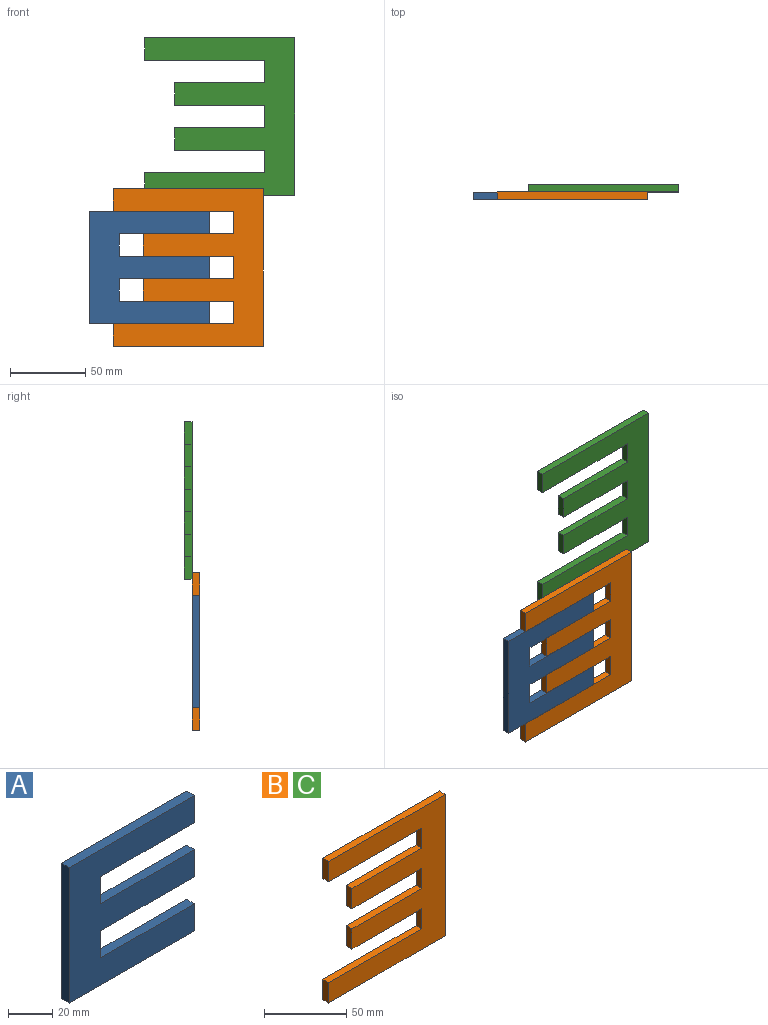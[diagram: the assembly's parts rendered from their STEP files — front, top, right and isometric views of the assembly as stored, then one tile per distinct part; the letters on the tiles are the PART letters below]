
ASSEMBLY  parts=3 mates=3
PART A: 14 faces, bbox 80x5x75 mm
  f0: plane 15x5mm, normal (1,0,0), area 75mm2, adj f1,f11,f12,f13
  f1: plane 60x5mm, normal (0,0,-1), area 300mm2, adj f0,f2,f12,f13
  f2: plane 15x5mm, normal (1,0,0), area 75mm2, adj f1,f3,f12,f13
  f3: plane 60x5mm, normal (0,0,1), area 300mm2, adj f2,f4,f12,f13
  f4: plane 15x5mm, normal (1,0,0), area 75mm2, adj f3,f5,f12,f13
  f5: plane 60x5mm, normal (0,0,-1), area 300mm2, adj f4,f6,f12,f13
  f6: plane 15x5mm, normal (1,0,0), area 75mm2, adj f5,f7,f12,f13
  f7: plane 80x5mm, normal (0,0,1), area 400mm2, adj f6,f8,f12,f13
  f8: plane 75x5mm, normal (-1,0,0), area 375mm2, adj f7,f9,f12,f13
  f9: plane 80x5mm, normal (0,0,-1), area 400mm2, adj f8,f10,f12,f13
  f10: plane 15x5mm, normal (1,0,0), area 75mm2, adj f9,f11,f12,f13
  f11: plane 60x5mm, normal (0,0,1), area 300mm2, adj f0,f10,f12,f13
  f12: plane 80x75mm, normal (0,-1,0), area 4200mm2, adj f0,f1,f2,f3,f4,f5,f6,f7
  f13: plane 80x75mm, normal (0,1,0), area 4200mm2, adj f0,f1,f2,f3,f4,f5,f6,f7
PART B: 18 faces, bbox 100x5x105 mm
  f0: plane 60x5mm, normal (0,0,1), area 300mm2, adj f1,f15,f16,f17
  f1: plane 15x5mm, normal (-1,0,0), area 75mm2, adj f0,f2,f16,f17
  f2: plane 60x5mm, normal (0,0,-1), area 300mm2, adj f1,f3,f16,f17
  f3: plane 15x5mm, normal (-1,0,0), area 75mm2, adj f2,f4,f16,f17
  f4: plane 80x5mm, normal (0,0,1), area 400mm2, adj f3,f5,f16,f17
  f5: plane 15x5mm, normal (-1,0,0), area 75mm2, adj f4,f6,f16,f17
  f6: plane 100x5mm, normal (0,0,-1), area 500mm2, adj f5,f7,f16,f17
  f7: plane 105x5mm, normal (1,0,0), area 525mm2, adj f6,f8,f16,f17
  f8: plane 100x5mm, normal (0,0,1), area 500mm2, adj f7,f9,f16,f17
  f9: plane 15x5mm, normal (-1,0,0), area 75mm2, adj f8,f10,f16,f17
  f10: plane 80x5mm, normal (0,0,-1), area 400mm2, adj f9,f11,f16,f17
  f11: plane 15x5mm, normal (-1,0,0), area 75mm2, adj f10,f12,f16,f17
  f12: plane 60x5mm, normal (0,0,1), area 300mm2, adj f11,f13,f16,f17
  f13: plane 15x5mm, normal (-1,0,0), area 75mm2, adj f12,f14,f16,f17
  f14: plane 60x5mm, normal (0,0,-1), area 300mm2, adj f13,f15,f16,f17
  f15: plane 15x5mm, normal (-1,0,0), area 75mm2, adj f0,f14,f16,f17
  f16: plane 105x100mm, normal (0,-1,0), area 6300mm2, adj f0,f1,f2,f3,f4,f5,f6,f7
  f17: plane 105x100mm, normal (0,1,0), area 6300mm2, adj f0,f1,f2,f3,f4,f5,f6,f7
PART C: same geometry as B
PLACE A t=(-104.59,-55.61,-10.92)mm
PLACE B t=(-95.25,-55.61,-11.6)mm fixed
PLACE C t=(-74.43,-50.61,89.04)mm
MATE planar B.f17 <-> C.f16  axis (0,1,0) through (-56.17,-55.61,-3.42)mm
MATE planar B.f12 <-> A.f5  axis (0,0,1) through (-86.17,-58.11,11.58)mm
MATE planar B.f16 <-> A.f12  axis (0,-1,0) through (-56.17,-60.61,26.58)mm
